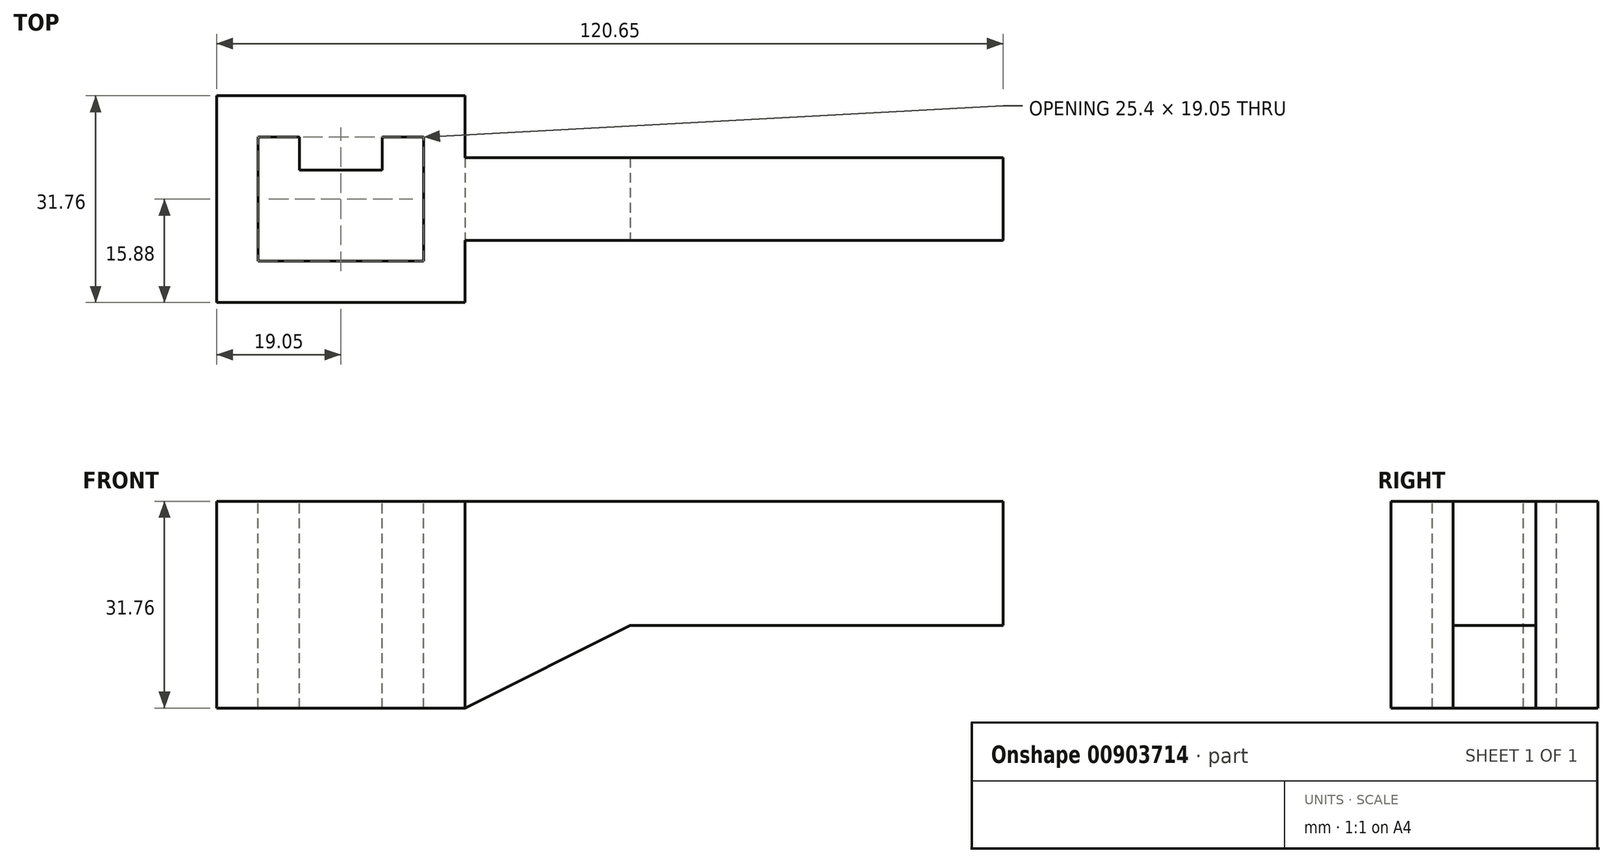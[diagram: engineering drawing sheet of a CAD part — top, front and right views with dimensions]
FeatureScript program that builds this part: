
annotation { "Feature Type Name" : "Feature", "Feature Type Description" : "" }
export const myFeature = defineFeature(function(context is Context, id is Id, definition is map)
    precondition{}
    {
        {
            var Q0;
            Q0=qCreatedBy(makeId("Front.planeOp"),FACE);
            var sketch = newSketch(context, id + "F0", { "sketchPlane" : qUnion([Q0])});
            skLineSegment(sketch, "E0.bottom", {"start": v(88.9, -9.52) * mm, "end": v(-88.9, -9.53) * mm});
            skLineSegment(sketch, "E0.top", {"start": v(88.9, 9.53) * mm, "end": v(-88.9, 9.52) * mm});
            skLineSegment(sketch, "E0.left", {"start": v(88.9, -9.52) * mm, "end": v(88.9, 9.53) * mm});
            skLineSegment(sketch, "E0.right", {"start": v(-88.9, -9.53) * mm, "end": v(-88.9, 9.52) * mm});
            skPoint(sketch, "E0.middle", {"position": v(0, 0) * mm});
            skSolve(sketch);
        }
        {
            var Q0;
            Q0=makeQuery(id+"F0.imprint","IMPRINT",FACE,{"disambiguationData":[TD([[makeQuery(id+"F0.imprint","IMPRINT",EDGE,{"derivedFrom":sQuery(id+"F0.wireOp",EDGE,"E0.bottom")}),-1.0]])]});
            extrude(context, id + "F1", {"entities" : qUnion([Q0]), "endBound" : BoundingType.SYMMETRIC, "depth" : 12.7 * mm, "offsetDistance" : 25.4 * mm});
        }
        {
            var Q0;
            Q0=makeQuery(id+"F1.opExtrude","SWEPT_FACE",FACE,{"disambiguationData":[OSD([sQuery(id+"F0.wireOp",EDGE,"E0.top")])]});
            var sketch = newSketch(context, id + "F2", { "sketchPlane" : qUnion([Q0])});
            skLineSegment(sketch, "E1.bottom", {"start": v(-88.9, 9.53) * mm, "end": v(-63.5, 9.53) * mm});
            skLineSegment(sketch, "E1.top", {"start": v(-88.9, -9.53) * mm, "end": v(-63.5, -9.52) * mm});
            skLineSegment(sketch, "E1.left", {"start": v(-88.9, 9.53) * mm, "end": v(-88.9, -9.52) * mm});
            skLineSegment(sketch, "E1.right", {"start": v(-63.5, 9.53) * mm, "end": v(-63.5, -9.52) * mm});
            skPoint(sketch, "E1.middle", {"position": v(-76.2, 0) * mm});
            skLineSegment(sketch, "E2.bottom", {"start": v(-57.15, -15.88) * mm, "end": v(-95.25, -15.88) * mm});
            skLineSegment(sketch, "E2.top", {"start": v(-57.15, 15.88) * mm, "end": v(-95.25, 15.87) * mm});
            skLineSegment(sketch, "E2.left", {"start": v(-57.15, -15.88) * mm, "end": v(-57.15, 15.88) * mm});
            skLineSegment(sketch, "E2.right", {"start": v(-95.25, -15.88) * mm, "end": v(-95.25, 15.87) * mm});
            skSolve(sketch);
        }
        {
            var Q0;
            Q0 = qSketchRegion(id + "F2", true);
            extrude(context, id + "F3", {"entities" : qUnion([Q0]), "operationType" : NewBodyOperationType.ADD, "oppositeDirection" : true, "depth" : 31.75 * mm, "offsetDistance" : 25.4 * mm});
        }
        {
            var Q0;
            Q0=makeQuery(id+"F3.boolean.opBoolean","MERGE",FACE,{"derivedFrom":[makeQuery(id+"F1.opExtrude","SWEPT_FACE",FACE,{"disambiguationData":[OSD([sQuery(id+"F0.wireOp",EDGE,"E0.top")])]}),makeQuery(id+"F3.opExtrude","CAP_FACE",FACE,{"disambiguationData":[OSD([sQuery(id+"F2.wireOp",EDGE,"E1.bottom"),sQuery(id+"F2.wireOp",EDGE,"E1.top"),sQuery(id+"F2.wireOp",EDGE,"E1.left"),sQuery(id+"F2.wireOp",EDGE,"E1.right"),sQuery(id+"F2.wireOp",EDGE,"E2.bottom"),sQuery(id+"F2.wireOp",EDGE,"E2.top"),sQuery(id+"F2.wireOp",EDGE,"E2.left"),sQuery(id+"F2.wireOp",EDGE,"E2.right")])],"isStart":true})]});
            var sketch = newSketch(context, id + "F4", { "sketchPlane" : qUnion([Q0])});
            skLineSegment(sketch, "E3.bottom", {"start": v(-88.9, 9.53) * mm, "end": v(-63.5, 9.53) * mm});
            skLineSegment(sketch, "E3.top", {"start": v(-88.9, -9.52) * mm, "end": v(-63.5, -9.52) * mm});
            skLineSegment(sketch, "E3.left", {"start": v(-88.9, 9.53) * mm, "end": v(-88.9, -9.52) * mm});
            skLineSegment(sketch, "E3.right", {"start": v(-63.5, 9.53) * mm, "end": v(-63.5, -9.52) * mm});
            skSolve(sketch);
        }
        {
            var Q0;
            Q0 = qSketchRegion(id + "F4", true);
            extrude(context, id + "F5", {"entities" : qUnion([Q0]), "operationType" : NewBodyOperationType.REMOVE, "oppositeDirection" : true, "depth" : 127 * mm, "offsetDistance" : 25.4 * mm});
        }
        {
            var Q0;
            Q0=makeQuery(id+"F3.boolean.opBoolean","MERGE",FACE,{"derivedFrom":[makeQuery(id+"F1.opExtrude","SWEPT_FACE",FACE,{"disambiguationData":[OSD([sQuery(id+"F0.wireOp",EDGE,"E0.top")])]}),makeQuery(id+"F3.opExtrude","CAP_FACE",FACE,{"disambiguationData":[OSD([sQuery(id+"F2.wireOp",EDGE,"E1.bottom"),sQuery(id+"F2.wireOp",EDGE,"E1.top"),sQuery(id+"F2.wireOp",EDGE,"E1.left"),sQuery(id+"F2.wireOp",EDGE,"E1.right"),sQuery(id+"F2.wireOp",EDGE,"E2.bottom"),sQuery(id+"F2.wireOp",EDGE,"E2.top"),sQuery(id+"F2.wireOp",EDGE,"E2.left"),sQuery(id+"F2.wireOp",EDGE,"E2.right")])],"isStart":true})]});
            var sketch = newSketch(context, id + "F6", { "sketchPlane" : qUnion([Q0])});
            skLineSegment(sketch, "E4.bottom", {"start": v(-69.85, 9.53) * mm, "end": v(-82.55, 9.53) * mm});
            skLineSegment(sketch, "E4.top", {"start": v(-69.85, 4.45) * mm, "end": v(-82.55, 4.44) * mm});
            skLineSegment(sketch, "E4.left", {"start": v(-69.85, 9.53) * mm, "end": v(-69.85, 4.45) * mm});
            skLineSegment(sketch, "E4.right", {"start": v(-82.55, 9.52) * mm, "end": v(-82.55, 4.45) * mm});
            skPoint(sketch, "E4.middle", {"position": v(-76.2, 6.99) * mm});
            skPoint(sketch, "E4.middle.positionSnap0", {"position": v(-76.2, 9.53) * mm});
            skPoint(sketch, "E4.centerSnap0", {"position": v(-76.2, 9.53) * mm});
            skSolve(sketch);
        }
        {
            var Q0;
            Q0 = qSketchRegion(id + "F6", true);
            extrude(context, id + "F7", {"entities" : qUnion([Q0]), "operationType" : NewBodyOperationType.ADD, "oppositeDirection" : true, "depth" : 31.75 * mm, "offsetDistance" : 25.4 * mm});
        }
        {
            var Q0;
            {var subQ1=sQuery(id+"F0.wireOp",EDGE,"E0.left");var subQ2=sQuery(id+"F0.wireOp",EDGE,"E0.top");var subQ3=sQuery(id+"F0.wireOp",EDGE,"E0.bottom");Q0=makeQuery(id+"F3.boolean.opBoolean","SPLIT",FACE,{"disambiguationData":[TD([makeQuery(id+"F1.opExtrude","SWEPT_FACE",FACE,{"disambiguationData":[OSD([subQ1])]})])],"derivedFrom":makeQuery(id+"F1.opExtrude","CAP_FACE",FACE,{"disambiguationData":[OSD([subQ3,subQ2,subQ1,sQuery(id+"F0.wireOp",EDGE,"E0.right")])],"isStart":false})});}
            var sketch = newSketch(context, id + "F8", { "sketchPlane" : qUnion([Q0])});
            skLineSegment(sketch, "E5", {"start": v(-31.83, -9.53) * mm, "end": v(-57.15, -9.53) * mm});
            skLineSegment(sketch, "E6", {"start": v(-57.15, -9.53) * mm, "end": v(-57.15, -22.23) * mm});
            skLineSegment(sketch, "E7", {"start": v(-57.15, -22.23) * mm, "end": v(-31.83, -9.53) * mm});
            skSolve(sketch);
        }
        {
            var Q0;
            Q0 = qSketchRegion(id + "F8", true);
            extrude(context, id + "F9", {"entities" : qUnion([Q0]), "operationType" : NewBodyOperationType.ADD, "oppositeDirection" : true, "depth" : 12.7 * mm, "offsetDistance" : 25.4 * mm});
        }
        {
            var Q0;
            Q0=makeQuery(id+"F7.boolean.opBoolean","MERGE",FACE,{"derivedFrom":[makeQuery(id+"F3.boolean.opBoolean","MERGE",FACE,{"derivedFrom":[makeQuery(id+"F1.opExtrude","SWEPT_FACE",FACE,{"disambiguationData":[OSD([sQuery(id+"F0.wireOp",EDGE,"E0.top")])]}),makeQuery(id+"F3.opExtrude","CAP_FACE",FACE,{"disambiguationData":[OSD([sQuery(id+"F2.wireOp",EDGE,"E1.bottom"),sQuery(id+"F2.wireOp",EDGE,"E1.top"),sQuery(id+"F2.wireOp",EDGE,"E1.left"),sQuery(id+"F2.wireOp",EDGE,"E1.right"),sQuery(id+"F2.wireOp",EDGE,"E2.bottom"),sQuery(id+"F2.wireOp",EDGE,"E2.top"),sQuery(id+"F2.wireOp",EDGE,"E2.left"),sQuery(id+"F2.wireOp",EDGE,"E2.right")])],"isStart":true})]}),makeQuery(id+"F7.opExtrude","CAP_FACE",FACE,{"disambiguationData":[OSD([sQuery(id+"F6.wireOp",EDGE,"E4.bottom"),sQuery(id+"F6.wireOp",EDGE,"E4.top"),sQuery(id+"F6.wireOp",EDGE,"E4.left"),sQuery(id+"F6.wireOp",EDGE,"E4.right")])],"isStart":true})]});
            var sketch = newSketch(context, id + "F10", { "sketchPlane" : qUnion([Q0])});
            skLineSegment(sketch, "E8.bottom", {"start": v(25.4, -6.35) * mm, "end": v(-57.15, -6.35) * mm});
            skLineSegment(sketch, "E8.top", {"start": v(25.4, 6.35) * mm, "end": v(-57.15, 6.35) * mm});
            skLineSegment(sketch, "E8.left", {"start": v(25.4, -6.35) * mm, "end": v(25.4, 6.35) * mm});
            skLineSegment(sketch, "E8.right", {"start": v(-57.15, -6.35) * mm, "end": v(-57.15, 6.35) * mm});
            skLineSegment(sketch, "E9.bottom", {"start": v(25.4, 6.35) * mm, "end": v(88.9, 6.35) * mm});
            skLineSegment(sketch, "E9.top", {"start": v(25.4, -6.35) * mm, "end": v(88.9, -6.35) * mm});
            skLineSegment(sketch, "E9.left", {"start": v(25.4, 6.35) * mm, "end": v(25.4, -6.35) * mm});
            skLineSegment(sketch, "E9.right", {"start": v(88.9, 6.35) * mm, "end": v(88.9, -6.35) * mm});
            skSolve(sketch);
        }
        {
            var Q0;
            Q0=makeQuery(id+"F10.imprint","IMPRINT",FACE,{"disambiguationData":[TD([[makeQuery(id+"F10.imprint","IMPRINT",EDGE,{"derivedFrom":sQuery(id+"F10.wireOp",EDGE,"E9.bottom")}),1.0]])]});
            extrude(context, id + "F11", {"entities" : qUnion([Q0]), "operationType" : NewBodyOperationType.REMOVE, "endBound" : BoundingType.THROUGH_ALL, "oppositeDirection" : true, "depth" : 25.4 * mm, "offsetDistance" : 25.4 * mm});
        }
    });
